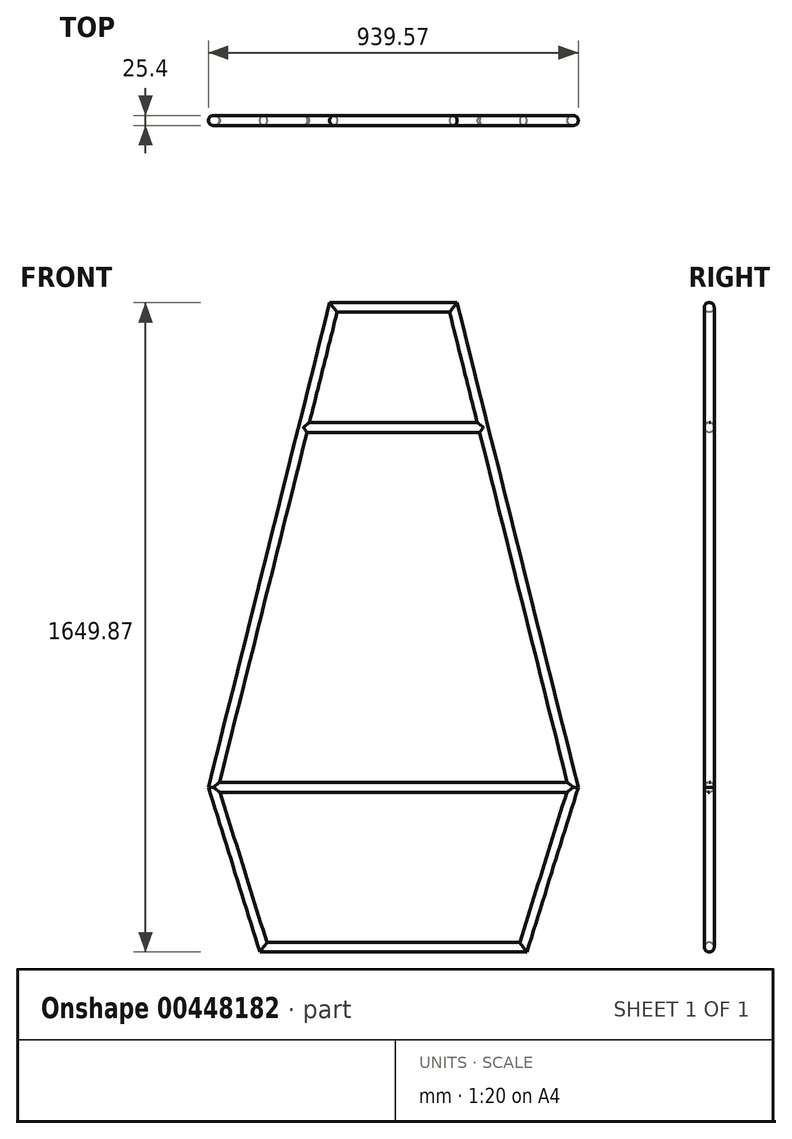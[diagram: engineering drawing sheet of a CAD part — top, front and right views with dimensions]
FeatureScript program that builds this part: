
annotation { "Feature Type Name" : "Feature", "Feature Type Description" : "" }
export const myFeature = defineFeature(function(context is Context, id is Id, definition is map)
    precondition{}
    {
        {
            var Q0;
            Q0=qCreatedBy(makeId("Front.planeOp"),FACE);
            var sketch = newSketch(context, id + "F0", { "sketchPlane" : qUnion([Q0])});
            skLineSegment(sketch, "E0", {"start": v(-330.23, -406.4) * mm, "end": v(330.17, -406.42) * mm});
            skLineSegment(sketch, "E1", {"start": v(-457.22, 0.01) * mm, "end": v(-330.23, -406.4) * mm});
            skLineSegment(sketch, "E2", {"start": v(457.18, -0.02) * mm, "end": v(330.17, -406.42) * mm});
            skLineSegment(sketch, "E3", {"start": v(-457.22, 0.01) * mm, "end": v(457.18, -0.02) * mm});
            skLineSegment(sketch, "E4", {"start": v(-152.42, 1219.2) * mm, "end": v(-457.22, 0.01) * mm});
            skLineSegment(sketch, "E5", {"start": v(152.38, 1219.2) * mm, "end": v(457.18, -0.02) * mm});
            skLineSegment(sketch, "E6", {"start": v(-152.42, 1219.2) * mm, "end": v(152.38, 1219.2) * mm});
            skLineSegment(sketch, "E7", {"start": v(0, 914.4) * mm, "end": v(-228.62, 914.42) * mm});
            skLineSegment(sketch, "E8", {"start": v(-228.62, 914.42) * mm, "end": v(228.58, 914.4) * mm});
            skCircle(sketch, "E9", {"center": v(-457.22, 0.01) * mm, "radius": 12.7 * mm});
            skCircle(sketch, "E10", {"center": v(457.18, -0.02) * mm, "radius": 12.7 * mm});
            skSolve(sketch);
        }
        {
            var Q0;
            Q0=qCreatedBy(makeId("Top.planeOp"),FACE);
            var sketch = newSketch(context, id + "F1", { "sketchPlane" : qUnion([Q0])});
            skCircle(sketch, "E11", {"center": v(-457.21, 0) * mm, "radius": 12.7 * mm});
            skSolve(sketch);
        }
        {
            var Q0;
            Q0 = qSketchRegion(id + "F1", true);
            var Q1;
            Q1=sQuery(id+"F0.wireOp",EDGE,"E4");
            var Q2;
            Q2=sQuery(id+"F0.wireOp",EDGE,"E6");
            var Q3;
            Q3=sQuery(id+"F0.wireOp",EDGE,"E5");
            var Q4;
            Q4=sQuery(id+"F0.wireOp",EDGE,"E2");
            var Q5;
            Q5=sQuery(id+"F0.wireOp",EDGE,"E0");
            var Q6;
            Q6=sQuery(id+"F0.wireOp",EDGE,"E1");
            sweep(context, id + "F2", {"profiles" : qUnion([Q0]), "path" : qUnion([Q1, Q2, Q3, Q4, Q5, Q6])});
        }
        {
            var Q0;
            Q0=qCreatedBy(makeId("Right.planeOp"),FACE);
            var sketch = newSketch(context, id + "F3", { "sketchPlane" : qUnion([Q0])});
            skCircle(sketch, "E12", {"center": v(0, 0) * mm, "radius": 12.7 * mm});
            skSolve(sketch);
        }
        {
            var Q0;
            Q0 = qSketchRegion(id + "F3", true);
            extrude(context, id + "F4", {"entities" : qUnion([Q0]), "operationType" : NewBodyOperationType.ADD, "depth" : 457.2 * mm, "hasSecondDirection" : true, "secondDirectionOppositeDirection" : true, "secondDirectionDepth" : 457.2 * mm});
        }
        {
            var Q0;
            Q0=qCreatedBy(makeId("Right.planeOp"),FACE);
            var sketch = newSketch(context, id + "F5", { "sketchPlane" : qUnion([Q0])});
            skCircle(sketch, "E13", {"center": v(0, 914.4) * mm, "radius": 12.7 * mm});
            skSolve(sketch);
        }
        {
            var Q0;
            Q0 = qSketchRegion(id + "F5", true);
            extrude(context, id + "F6", {"entities" : qUnion([Q0]), "operationType" : NewBodyOperationType.ADD, "depth" : 228.6 * mm, "hasSecondDirection" : true, "secondDirectionOppositeDirection" : true, "secondDirectionDepth" : 228.6 * mm});
        }
    });
